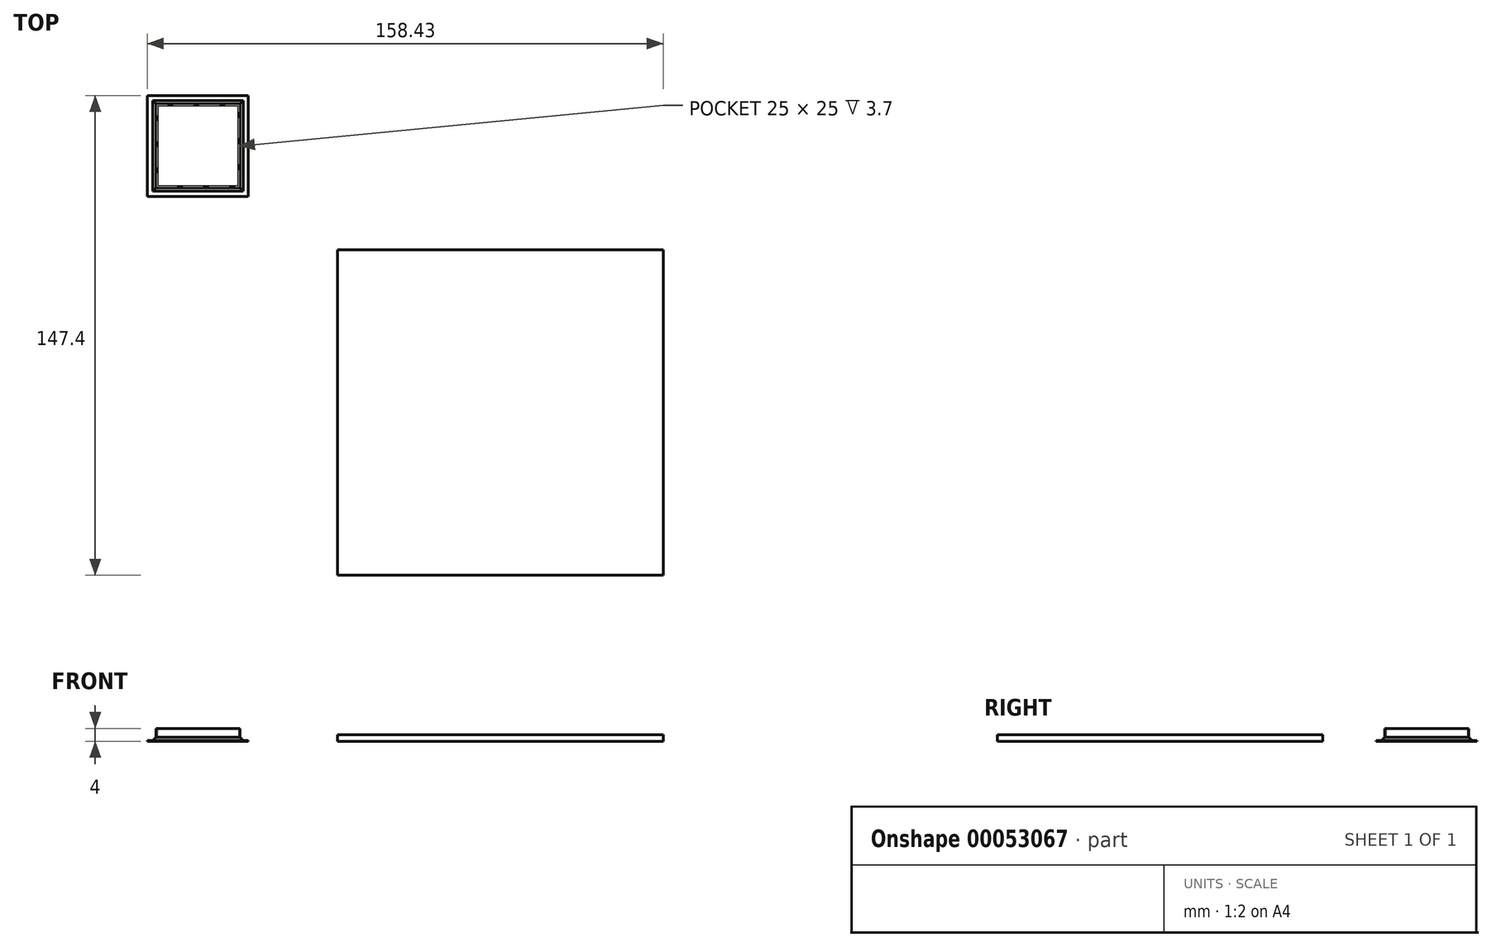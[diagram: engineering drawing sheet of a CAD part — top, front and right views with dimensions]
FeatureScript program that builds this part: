
annotation { "Feature Type Name" : "Feature", "Feature Type Description" : "" }
export const myFeature = defineFeature(function(context is Context, id is Id, definition is map)
    precondition{}
    {
        {
            var Q0;
            Q0=qCreatedBy(makeId("Top.planeOp"),FACE);
            var sketch = newSketch(context, id + "F0", { "sketchPlane" : qUnion([Q0])});
            skLineSegment(sketch, "E0.bottom", {"start": v(0, 0) * mm, "end": v(100, 0) * mm});
            skLineSegment(sketch, "E0.top", {"start": v(0, -100) * mm, "end": v(100, -100) * mm});
            skLineSegment(sketch, "E0.left", {"start": v(0, 0) * mm, "end": v(0, -100) * mm});
            skLineSegment(sketch, "E0.right", {"start": v(100, 0) * mm, "end": v(100, -100) * mm});
            skSolve(sketch);
        }
        {
            var Q0;
            Q0=makeQuery(id+"F0.imprint","IMPRINT",FACE,{"disambiguationData":[TD([[makeQuery(id+"F0.imprint","IMPRINT",EDGE,{"derivedFrom":sQuery(id+"F0.wireOp",EDGE,"E0.bottom")}),-1.0]])]});
            extrude(context, id + "F1", {"entities" : qUnion([Q0]), "depth" : 2 * mm});
        }
        {
            var Q0;
            Q0=qCreatedBy(makeId("Top.planeOp"),FACE);
            var sketch = newSketch(context, id + "F2", { "sketchPlane" : qUnion([Q0])});
            skLineSegment(sketch, "E1.bottom", {"start": v(-55.43, 44.4) * mm, "end": v(-30.43, 44.4) * mm});
            skLineSegment(sketch, "E1.top", {"start": v(-55.43, 19.4) * mm, "end": v(-30.43, 19.4) * mm});
            skLineSegment(sketch, "E1.left", {"start": v(-55.43, 44.4) * mm, "end": v(-55.43, 19.4) * mm});
            skLineSegment(sketch, "E1.right", {"start": v(-30.43, 44.4) * mm, "end": v(-30.43, 19.4) * mm});
            skLineSegment(sketch, "E2.0", {"start": v(-55.83, 44.8) * mm, "end": v(-30.03, 44.8) * mm});
            skLineSegment(sketch, "E2.1", {"start": v(-55.83, 44.8) * mm, "end": v(-55.83, 19) * mm});
            skLineSegment(sketch, "E2.2", {"start": v(-55.83, 19) * mm, "end": v(-30.03, 19) * mm});
            skLineSegment(sketch, "E2.3", {"start": v(-30.03, 44.8) * mm, "end": v(-30.03, 19) * mm});
            skLineSegment(sketch, "E3.0", {"start": v(-58.43, 47.4) * mm, "end": v(-27.43, 47.4) * mm});
            skLineSegment(sketch, "E3.1", {"start": v(-58.43, 47.4) * mm, "end": v(-58.43, 16.4) * mm});
            skLineSegment(sketch, "E3.2", {"start": v(-58.43, 16.4) * mm, "end": v(-27.43, 16.4) * mm});
            skLineSegment(sketch, "E3.3", {"start": v(-27.43, 47.4) * mm, "end": v(-27.43, 16.4) * mm});
            skSolve(sketch);
        }
        {
            var Q0;
            Q0=makeQuery(id+"F2.imprint","IMPRINT",FACE,{"disambiguationData":[TD([[makeQuery(id+"F2.imprint","IMPRINT",EDGE,{"derivedFrom":sQuery(id+"F2.wireOp",EDGE,"E1.bottom")}),1.0]])]});
            extrude(context, id + "F3", {"entities" : qUnion([Q0]), "depth" : 4 * mm});
        }
        {
            var Q0;
            Q0=makeQuery(id+"F2.imprint","IMPRINT",FACE,{"disambiguationData":[TD([[makeQuery(id+"F2.imprint","IMPRINT",EDGE,{"derivedFrom":sQuery(id+"F2.wireOp",EDGE,"E2.0")}),1.0]])]});
            var Q1;
            Q1=makeQuery(id+"F2.imprint","IMPRINT",FACE,{"disambiguationData":[TD([[makeQuery(id+"F2.imprint","IMPRINT",EDGE,{"derivedFrom":sQuery(id+"F2.wireOp",EDGE,"E1.bottom")}),-1.0]])]});
            var Q2;
            Q2=makeQuery(id+"F2.imprint","IMPRINT",FACE,{"disambiguationData":[TD([[makeQuery(id+"F2.imprint","IMPRINT",EDGE,{"derivedFrom":sQuery(id+"F2.wireOp",EDGE,"E1.bottom")}),1.0]])]});
            extrude(context, id + "F4", {"entities" : qUnion([Q0, Q1, Q2]), "operationType" : NewBodyOperationType.ADD, "depth" : .3 * mm});
        }
        {
            var Q0;
            Q0=makeQuery(id+"F4.boolean.opBoolean","INTERSECT",EDGE,{"derivedFrom":[makeQuery(id+"F3.opExtrude","SWEPT_FACE",FACE,{"disambiguationData":[OSD([sQuery(id+"F2.wireOp",EDGE,"E2.0")])]}),makeQuery(id+"F4.opExtrude","CAP_FACE",FACE,{"disambiguationData":[OSD([sQuery(id+"F2.wireOp",EDGE,"E3.0"),sQuery(id+"F2.wireOp",EDGE,"E3.1"),sQuery(id+"F2.wireOp",EDGE,"E3.2"),sQuery(id+"F2.wireOp",EDGE,"E3.3")])],"isStart":false})]});
            var Q1;
            Q1=makeQuery(id+"F4.boolean.opBoolean","INTERSECT",EDGE,{"derivedFrom":[makeQuery(id+"F3.opExtrude","SWEPT_FACE",FACE,{"disambiguationData":[OSD([sQuery(id+"F2.wireOp",EDGE,"E2.3")])]}),makeQuery(id+"F4.opExtrude","CAP_FACE",FACE,{"disambiguationData":[OSD([sQuery(id+"F2.wireOp",EDGE,"E3.0"),sQuery(id+"F2.wireOp",EDGE,"E3.1"),sQuery(id+"F2.wireOp",EDGE,"E3.2"),sQuery(id+"F2.wireOp",EDGE,"E3.3")])],"isStart":false})]});
            var Q2;
            Q2=makeQuery(id+"F4.boolean.opBoolean","INTERSECT",EDGE,{"derivedFrom":[makeQuery(id+"F3.opExtrude","SWEPT_FACE",FACE,{"disambiguationData":[OSD([sQuery(id+"F2.wireOp",EDGE,"E2.1")])]}),makeQuery(id+"F4.opExtrude","CAP_FACE",FACE,{"disambiguationData":[OSD([sQuery(id+"F2.wireOp",EDGE,"E3.0"),sQuery(id+"F2.wireOp",EDGE,"E3.1"),sQuery(id+"F2.wireOp",EDGE,"E3.2"),sQuery(id+"F2.wireOp",EDGE,"E3.3")])],"isStart":false})]});
            var Q3;
            Q3=makeQuery(id+"F4.boolean.opBoolean","INTERSECT",EDGE,{"derivedFrom":[makeQuery(id+"F3.opExtrude","SWEPT_FACE",FACE,{"disambiguationData":[OSD([sQuery(id+"F2.wireOp",EDGE,"E2.2")])]}),makeQuery(id+"F4.opExtrude","CAP_FACE",FACE,{"disambiguationData":[OSD([sQuery(id+"F2.wireOp",EDGE,"E3.0"),sQuery(id+"F2.wireOp",EDGE,"E3.1"),sQuery(id+"F2.wireOp",EDGE,"E3.2"),sQuery(id+"F2.wireOp",EDGE,"E3.3")])],"isStart":false})]});
            chamfer(context, id + "F5", {"entities" : qUnion([Q0, Q1, Q2, Q3]), "width" : 1 * mm, "tangentPropagation" : true});
        }
    });
